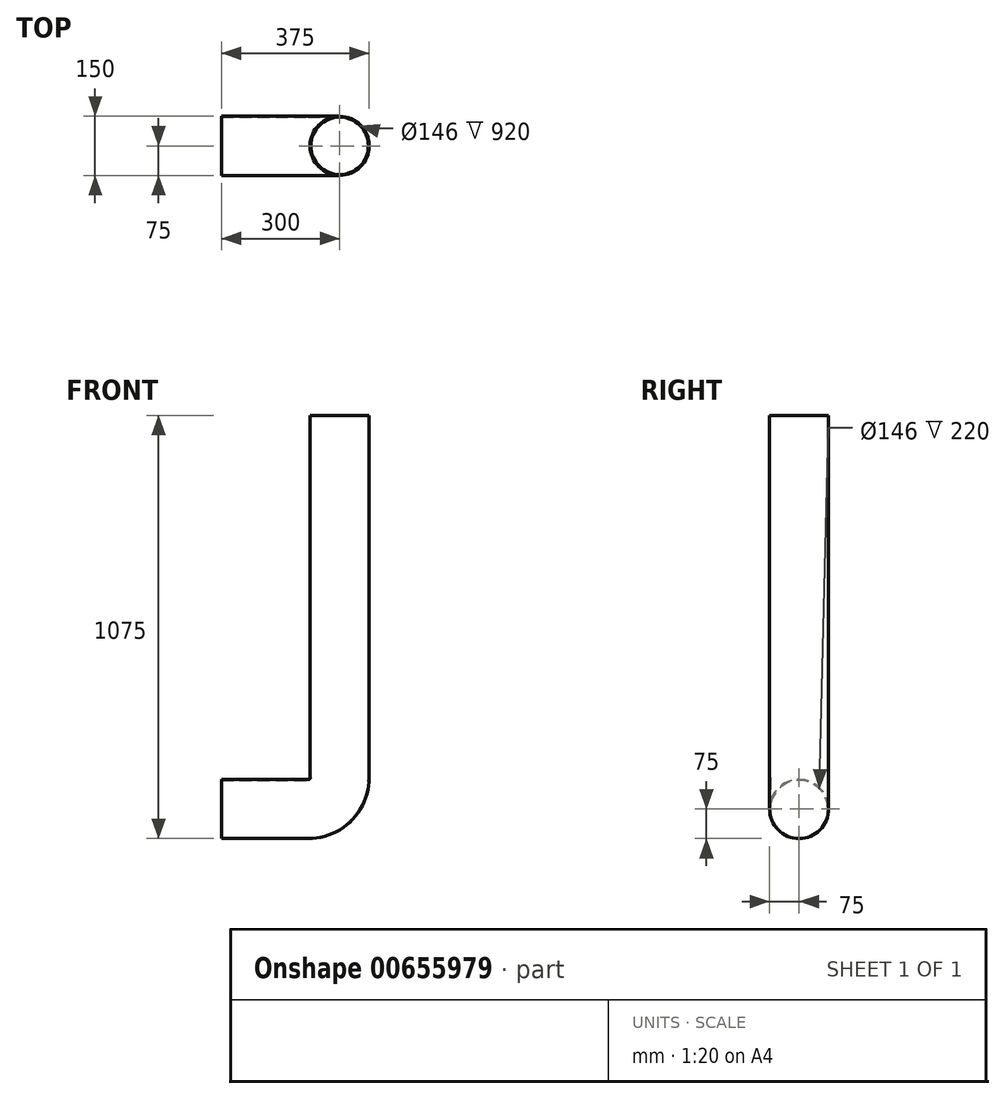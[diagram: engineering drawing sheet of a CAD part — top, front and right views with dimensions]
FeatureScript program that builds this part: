
annotation { "Feature Type Name" : "Feature", "Feature Type Description" : "" }
export const myFeature = defineFeature(function(context is Context, id is Id, definition is map)
    precondition{}
    {
        {
            var Q0;
            Q0=qCreatedBy(makeId("Right.planeOp"),FACE);
            var sketch = newSketch(context, id + "F0", { "sketchPlane" : qUnion([Q0])});
            skCircle(sketch, "E0", {"center": v(0, 0) * mm, "radius": 75 * mm});
            skCircle(sketch, "E1", {"center": v(0, 0) * mm, "radius": 73 * mm});
            skSolve(sketch);
        }
        {
            var Q0;
            Q0=qCreatedBy(makeId("Front.planeOp"),FACE);
            var sketch = newSketch(context, id + "F1", { "sketchPlane" : qUnion([Q0])});
            skLineSegment(sketch, "E2", {"start": v(0, 0) * mm, "end": v(220, 0) * mm});
            skLineSegment(sketch, "E3", {"start": v(300, 80) * mm, "end": v(300, 1000) * mm});
            skPoint(sketch, "E4.visualSharp", {"position": v(300, 0) * mm});
            skArc(sketch, "E4.filletArc", {"start": v(220, 0) * mm, "mid": v(276.57, 23.43) * mm, "end": v(300, 80) * mm});
            skSolve(sketch);
        }
        {
            var Q0;
            Q0=makeQuery(id+"F0.imprint","IMPRINT",FACE,{"disambiguationData":[TD([[makeQuery(id+"F0.imprint","IMPRINT",EDGE,{"derivedFrom":sQuery(id+"F0.wireOp",EDGE,"E0")}),1.0]])]});
            var Q1;
            Q1=sQuery(id+"F1.wireOp",EDGE,"E2");
            var Q2;
            Q2=sQuery(id+"F1.wireOp",EDGE,"E4.filletArc");
            var Q3;
            Q3=sQuery(id+"F1.wireOp",EDGE,"E3");
            sweep(context, id + "F2", {"profiles" : qUnion([Q0]), "path" : qUnion([Q1, Q2, Q3])});
        }
    });
